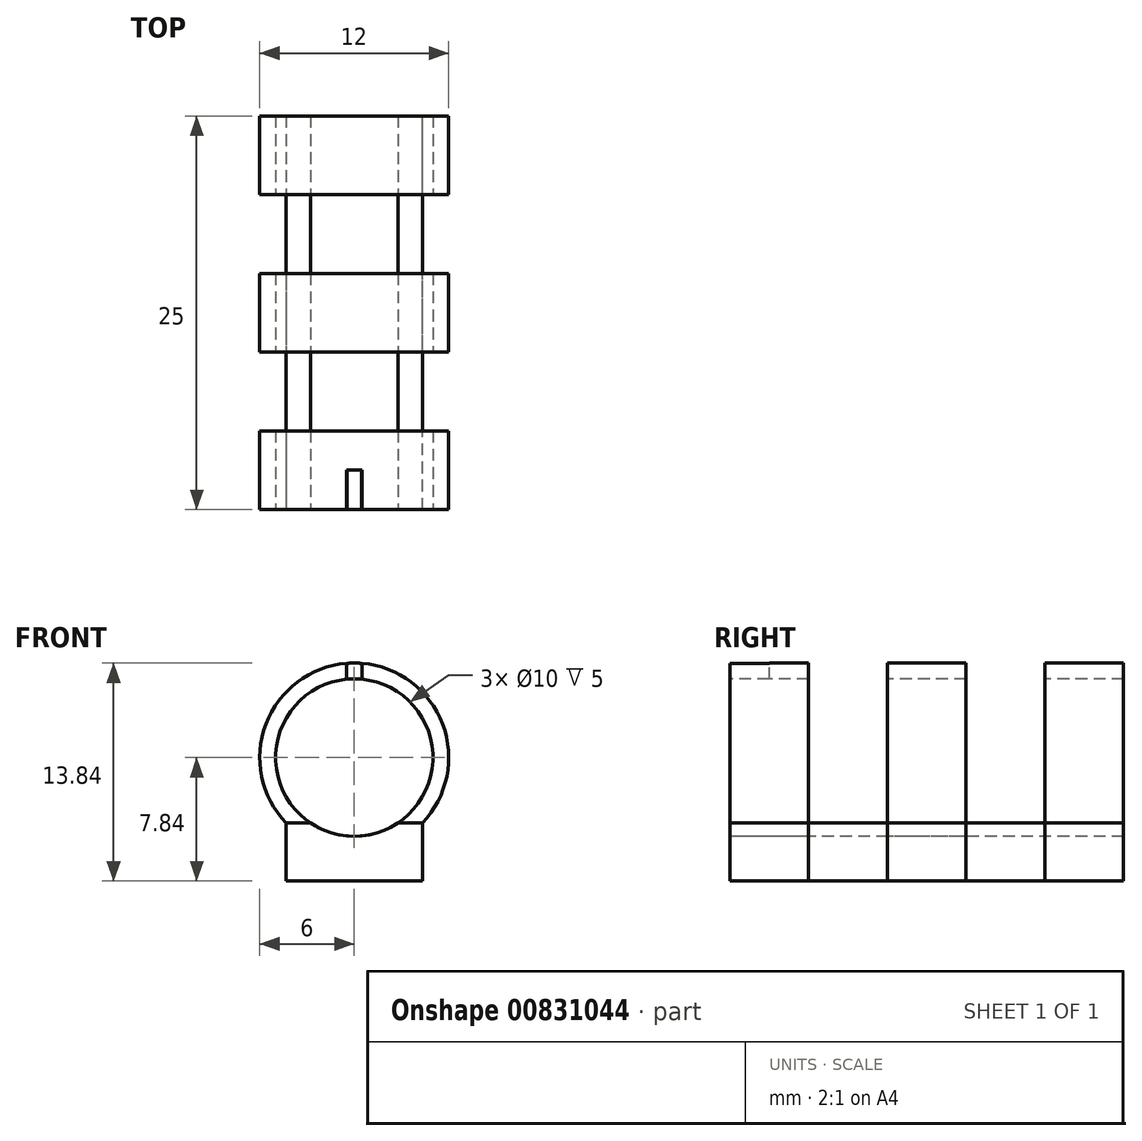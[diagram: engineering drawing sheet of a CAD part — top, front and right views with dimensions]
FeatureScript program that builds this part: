
annotation { "Feature Type Name" : "Feature", "Feature Type Description" : "" }
export const myFeature = defineFeature(function(context is Context, id is Id, definition is map)
    precondition{}
    {
        {
            var Q0;
            Q0=qCreatedBy(makeId("Front.planeOp"),FACE);
            var sketch = newSketch(context, id + "F0", { "sketchPlane" : qUnion([Q0])});
            skCircle(sketch, "E0", {"center": v(0, 0) * mm, "radius": 6 * mm});
            skSolve(sketch);
        }
        {
            var Q0;
            Q0 = qSketchRegion(id + "F0", true);
            extrude(context, id + "F1", {"entities" : qUnion([Q0]), "depth" : 30 * mm, "offsetDistance" : 25 * mm});
        }
        {
            var Q0;
            Q0=makeQuery(id+"F1.opExtrude","CAP_FACE",FACE,{"disambiguationData":[OSD([sQuery(id+"F0.wireOp",EDGE,"E0")])],"isStart":false});
            var sketch = newSketch(context, id + "F2", { "sketchPlane" : qUnion([Q0])});
            skLineSegment(sketch, "E1.bottom", {"start": v(-4.32, -4.16) * mm, "end": v(4.32, -4.16) * mm});
            skLineSegment(sketch, "E1.top", {"start": v(-4.32, -7.84) * mm, "end": v(4.32, -7.84) * mm});
            skLineSegment(sketch, "E1.left", {"start": v(-4.32, -4.16) * mm, "end": v(-4.32, -7.84) * mm});
            skLineSegment(sketch, "E1.right", {"start": v(4.32, -4.16) * mm, "end": v(4.32, -7.84) * mm});
            skPoint(sketch, "E1.middle", {"position": v(0, -6) * mm});
            skSolve(sketch);
        }
        {
            var Q0;
            Q0 = qSketchRegion(id + "F2", true);
            var Q1;
            Q1=makeQuery(id+"F1.opExtrude","CAP_FACE",FACE,{"disambiguationData":[OSD([sQuery(id+"F0.wireOp",EDGE,"E0")])],"isStart":true});
            extrude(context, id + "F3", {"entities" : qUnion([Q0]), "operationType" : NewBodyOperationType.ADD, "endBound" : BoundingType.UP_TO_SURFACE, "oppositeDirection" : true, "depth" : 31 * mm, "endBoundEntityFace" : qUnion([Q1]), "offsetDistance" : 25 * mm});
        }
        {
            var Q0;
            Q0=makeQuery(id+"F1.opExtrude","CAP_FACE",FACE,{"disambiguationData":[OSD([sQuery(id+"F0.wireOp",EDGE,"E0")])],"isStart":false});
            var sketch = newSketch(context, id + "F4", { "sketchPlane" : qUnion([Q0])});
            skCircle(sketch, "E2", {"center": v(0, 0) * mm, "radius": 5 * mm});
            skSolve(sketch);
        }
        {
            var Q0;
            Q0=qCreatedBy(makeId("Top.planeOp"),FACE);
            var sketch = newSketch(context, id + "F5", { "sketchPlane" : qUnion([Q0])});
            skLineSegment(sketch, "E3.0", {"start": v(6, -30) * mm, "end": v(-6, -30) * mm});
            skLineSegment(sketch, "E4.bottom", {"start": v(-6, -20) * mm, "end": v(6, -20) * mm});
            skLineSegment(sketch, "E4.top", {"start": v(-6, -25) * mm, "end": v(6, -25) * mm});
            skLineSegment(sketch, "E4.left", {"start": v(-6, -20) * mm, "end": v(-6, -25) * mm});
            skLineSegment(sketch, "E4.right", {"start": v(6, -20) * mm, "end": v(6, -25) * mm});
            skPoint(sketch, "E4.middle", {"position": v(0, -22.5) * mm});
            skLineSegment(sketch, "E5.0", {"start": v(6, 0) * mm, "end": v(-6, 0) * mm});
            skLineSegment(sketch, "E6.bottom", {"start": v(6, -15) * mm, "end": v(-6, -15) * mm});
            skLineSegment(sketch, "E6.top", {"start": v(6, -10) * mm, "end": v(-6, -10) * mm});
            skLineSegment(sketch, "E6.left", {"start": v(6, -15) * mm, "end": v(6, -10) * mm});
            skLineSegment(sketch, "E6.right", {"start": v(-6, -15) * mm, "end": v(-6, -10) * mm});
            skPoint(sketch, "E6.middle", {"position": v(0, -12.5) * mm});
            skLineSegment(sketch, "E7.bottom", {"start": v(6, -5) * mm, "end": v(-6, -5) * mm});
            skLineSegment(sketch, "E7.left", {"start": v(6, -5) * mm, "end": v(6, 0) * mm});
            skLineSegment(sketch, "E7.right", {"start": v(-6, -5) * mm, "end": v(-6, 0) * mm});
            skPoint(sketch, "E7.middle", {"position": v(0, -2.5) * mm});
            skSolve(sketch);
        }
        {
            var Q0;
            Q0 = qSketchRegion(id + "F5", true);
            var Q1;
            Q1=makeQuery(id+"F3.opExtrude","SWEPT_FACE",FACE,{"disambiguationData":[OSD([sQuery(id+"F2.wireOp",EDGE,"E1.top")])]});
            extrude(context, id + "F6", {"entities" : qUnion([Q0]), "operationType" : NewBodyOperationType.REMOVE, "endBound" : BoundingType.UP_TO_SURFACE, "oppositeDirection" : true, "depth" : 25 * mm, "endBoundEntityFace" : qUnion([Q1]), "offsetDistance" : 25 * mm, "hasSecondDirection" : true, "secondDirectionOppositeDirection" : false, "secondDirectionDepth" : 25 * mm});
        }
        {
            var Q0;
            Q0=makeQuery(id+"F6.boolean.opBoolean","SPLIT",FACE,{"disambiguationData":[TD([makeQuery(id+"F6.opExtrude","SWEPT_FACE",FACE,{"disambiguationData":[OSD([sQuery(id+"F5.wireOp",EDGE,"E4.bottom")])]})])],"derivedFrom":makeQuery(id+"F3.opExtrude","SWEPT_FACE",FACE,{"disambiguationData":[OSD([sQuery(id+"F2.wireOp",EDGE,"E1.left")])]})});
            var sketch = newSketch(context, id + "F7", { "sketchPlane" : qUnion([Q0])});
            skPoint(sketch, "E8.0", {"position": v(5, -4.16) * mm});
            skPoint(sketch, "E8.1", {"position": v(30, -7.84) * mm});
            skLineSegment(sketch, "E9.bottom", {"start": v(5, -4.16) * mm, "end": v(30, -4.16) * mm});
            skLineSegment(sketch, "E9.top", {"start": v(5, -7.84) * mm, "end": v(30, -7.84) * mm});
            skLineSegment(sketch, "E9.left", {"start": v(5, -4.16) * mm, "end": v(5, -7.84) * mm});
            skLineSegment(sketch, "E9.right", {"start": v(30, -4.16) * mm, "end": v(30, -7.84) * mm});
            skSolve(sketch);
        }
        {
            var Q0;
            Q0 = qSketchRegion(id + "F7", true);
            var Q1;
            Q1=makeQuery(id+"F6.boolean.opBoolean","SPLIT",FACE,{"disambiguationData":[TD([makeQuery(id+"F6.opExtrude","SWEPT_FACE",FACE,{"disambiguationData":[OSD([sQuery(id+"F5.wireOp",EDGE,"E6.top")])]})])],"derivedFrom":makeQuery(id+"F3.opExtrude","SWEPT_FACE",FACE,{"disambiguationData":[OSD([sQuery(id+"F2.wireOp",EDGE,"E1.right")])]})});
            extrude(context, id + "F8", {"entities" : qUnion([Q0]), "endBound" : BoundingType.UP_TO_SURFACE, "oppositeDirection" : true, "depth" : 25 * mm, "endBoundEntityFace" : qUnion([Q1]), "offsetDistance" : 25 * mm});
        }
        {
            var Q0;
            Q0 = qSketchRegion(id + "F4", true);
            extrude(context, id + "F9", {"entities" : qUnion([Q0]), "operationType" : NewBodyOperationType.REMOVE, "endBound" : BoundingType.THROUGH_ALL, "oppositeDirection" : true, "depth" : 25 * mm, "offsetDistance" : 25 * mm});
        }
        {
            var Q0;
            Q0=makeQuery(id+"F3.boolean.opBoolean","MERGE",FACE,{"derivedFrom":[makeQuery(id+"F1.opExtrude","CAP_FACE",FACE,{"disambiguationData":[OSD([sQuery(id+"F0.wireOp",EDGE,"E0")])],"isStart":false}),makeQuery(id+"F3.opExtrude","CAP_FACE",FACE,{"disambiguationData":[OSD([sQuery(id+"F2.wireOp",EDGE,"E1.bottom"),sQuery(id+"F2.wireOp",EDGE,"E1.top"),sQuery(id+"F2.wireOp",EDGE,"E1.left"),sQuery(id+"F2.wireOp",EDGE,"E1.right")])],"isStart":true})]});
            var sketch = newSketch(context, id + "F10", { "sketchPlane" : qUnion([Q0])});
            skLineSegment(sketch, "E10.bottom", {"start": v(-0.5, 6) * mm, "end": v(0.5, 6) * mm});
            skLineSegment(sketch, "E10.top", {"start": v(-0.5, 4.98) * mm, "end": v(0.5, 4.98) * mm});
            skLineSegment(sketch, "E10.left", {"start": v(-0.5, 6) * mm, "end": v(-0.5, 4.98) * mm});
            skLineSegment(sketch, "E10.right", {"start": v(0.5, 6) * mm, "end": v(0.5, 4.98) * mm});
            skPoint(sketch, "E10.middle", {"position": v(0, 5.49) * mm});
            skPoint(sketch, "E10.middle.positionSnap0", {"position": v(0, 6) * mm});
            skPoint(sketch, "E10.cornerSnap0", {"position": v(0, 6) * mm});
            skPoint(sketch, "E10.centerSnap0", {"position": v(0, 6) * mm});
            skSolve(sketch);
        }
        {
            var Q0;
            Q0 = qSketchRegion(id + "F10", true);
            var Q1;
            Q1=makeQuery(id+"F6.boolean.opBoolean","COPY",FACE,{"derivedFrom":makeQuery(id+"F6.opExtrude","SWEPT_FACE",FACE,{"disambiguationData":[OSD([sQuery(id+"F5.wireOp",EDGE,"E4.top")])]})});
            extrude(context, id + "F11", {"entities" : qUnion([Q0]), "operationType" : NewBodyOperationType.REMOVE, "endBound" : BoundingType.UP_TO_SURFACE, "oppositeDirection" : true, "depth" : 25 * mm, "endBoundEntityFace" : qUnion([Q1]), "hasOffset" : true, "offsetDistance" : 2.5 * mm});
        }
    });
